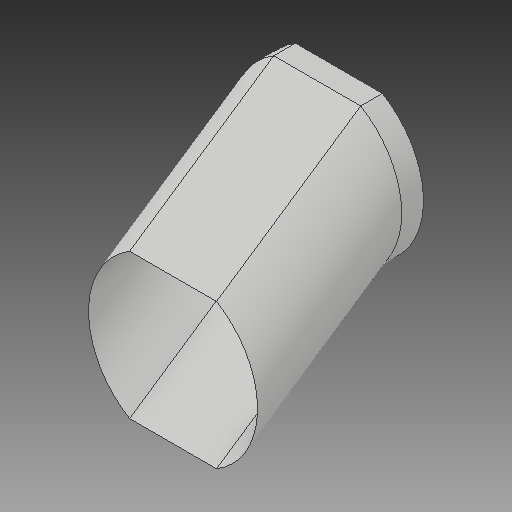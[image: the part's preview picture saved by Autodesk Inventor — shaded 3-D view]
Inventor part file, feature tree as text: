
AUTODESK INVENTOR PART (.ipt)
format: ipt  version: 2017 (Build 210142000, 142)  size: 122,880 bytes
history: native  units: in
note: dims shown in document units (in); Inventor stores cm internally (conversion verified against a paired STEP export)
features: sketch x2, extrude x1, plane x1, sweep x1, delete_face x1
ambient origin geometry x8: Origin, YZ Plane, XZ Plane, XY Plane, X Axis, Y Axis, Z Axis, Center Point
bodies: Solid1 (feature_tree)
feature tree (6):
  sketch  "Sketch1"  dims[d0=6.6667in d3=1.0in d4=0.0in d12=8.0in]
  extrude  "connecction top"  Depth=6.6667in
  plane  "Work Plane2"
  sweep  "ramp"
  delete_face  "Delete Face1"
  sketch  "Sketch6"  dims[d28=8.0in d45=0.0in d46=0.0in d65=0.8521in d66=4.0in d68=3.8873in d69=3.8873in d73=1.6458in d79=3.3333in]
